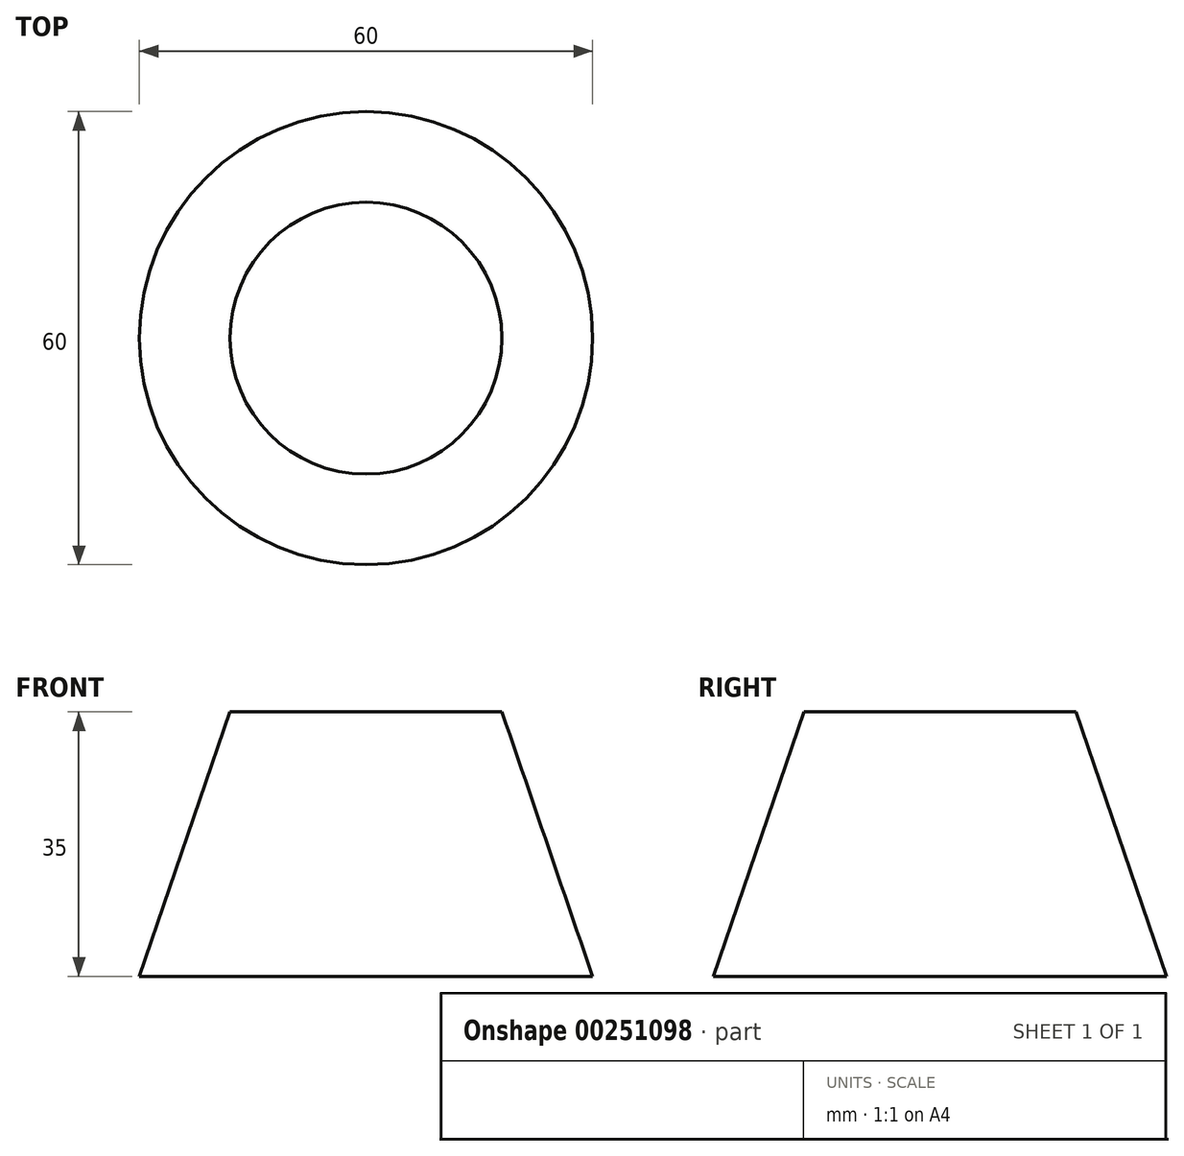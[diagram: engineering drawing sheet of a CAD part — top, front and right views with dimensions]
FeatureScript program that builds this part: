
annotation { "Feature Type Name" : "Feature", "Feature Type Description" : "" }
export const myFeature = defineFeature(function(context is Context, id is Id, definition is map)
    precondition{}
    {
        {
            var Q0;
            Q0=qCreatedBy(makeId("Front.planeOp"),FACE);
            var sketch = newSketch(context, id + "F0", { "sketchPlane" : qUnion([Q0])});
            skLineSegment(sketch, "E0", {"start": v(0, 0) * mm, "end": v(0, 35) * mm});
            skLineSegment(sketch, "E1", {"start": v(0, 35) * mm, "end": v(18, 35) * mm});
            skLineSegment(sketch, "E2", {"start": v(18, 35) * mm, "end": v(30, 0) * mm});
            skLineSegment(sketch, "E3", {"start": v(30, 0) * mm, "end": v(0, 0) * mm});
            skLineSegment(sketch, "E4", {"start": v(0, 62.76) * mm, "end": v(0, -45.3) * mm, "construction": true});
            skSolve(sketch);
        }
        {
            var Q0;
            Q0=makeQuery(id+"F0.imprint","IMPRINT",FACE,{"disambiguationData":[TD([[makeQuery(id+"F0.imprint","IMPRINT",EDGE,{"derivedFrom":sQuery(id+"F0.wireOp",EDGE,"E0")}),-1.0]])]});
            var Q1;
            Q1=sQuery(id+"F0.wireOp",EDGE,"E4");
            var Q2;
            Q2=sQuery(id+"F0.wireOp",EDGE,"E4");
            revolve(context, id + "F1", {"entities" : qUnion([Q0]), "surfaceEntities" : qUnion([Q1]), "axis" : qUnion([Q2]), "revolveType" : RevolveType.FULL});
        }
    });
